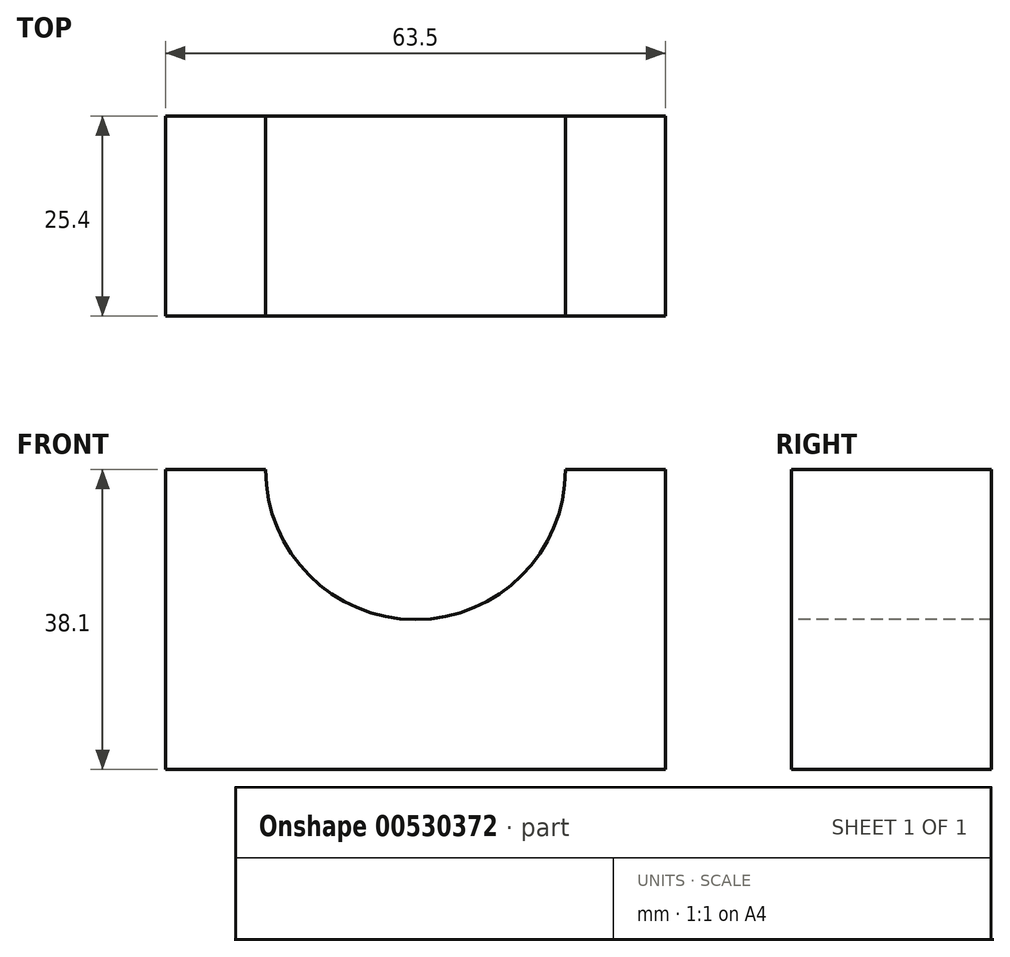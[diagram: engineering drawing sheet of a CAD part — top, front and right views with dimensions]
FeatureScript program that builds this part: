
annotation { "Feature Type Name" : "Feature", "Feature Type Description" : "" }
export const myFeature = defineFeature(function(context is Context, id is Id, definition is map)
    precondition{}
    {
        {
            var Q0;
            Q0=qCreatedBy(makeId("Front.planeOp"),FACE);
            var sketch = newSketch(context, id + "F0", { "sketchPlane" : qUnion([Q0])});
            skLineSegment(sketch, "E0", {"start": v(-63.5, 38.1) * mm, "end": v(-63.5, 0) * mm});
            skLineSegment(sketch, "E1", {"start": v(-63.5, 0) * mm, "end": v(0, 0) * mm});
            skLineSegment(sketch, "E2", {"start": v(0, 0) * mm, "end": v(0, 38.1) * mm});
            skLineSegment(sketch, "E3", {"start": v(0, 38.1) * mm, "end": v(-63.5, 38.1) * mm});
            skSolve(sketch);
        }
        {
            var Q0;
            Q0=makeQuery(id+"F0.imprint","IMPRINT",FACE,{"disambiguationData":[TD([[makeQuery(id+"F0.imprint","IMPRINT",EDGE,{"derivedFrom":sQuery(id+"F0.wireOp",EDGE,"E0")}),1.0]])]});
            extrude(context, id + "F1", {"entities" : qUnion([Q0]), "depth" : 25.4 * mm, "offsetDistance" : 25.4 * mm});
        }
        {
            var Q0;
            Q0=makeQuery(id+"F1.opExtrude","CAP_FACE",FACE,{"disambiguationData":[OSD([sQuery(id+"F0.wireOp",EDGE,"E0"),sQuery(id+"F0.wireOp",EDGE,"E1"),sQuery(id+"F0.wireOp",EDGE,"E2"),sQuery(id+"F0.wireOp",EDGE,"E3")])],"isStart":false});
            var sketch = newSketch(context, id + "F2", { "sketchPlane" : qUnion([Q0])});
            skArc(sketch, "E4", {"start": v(-50.8, 38.1) * mm, "mid": v(-31.75, 19.05) * mm, "end": v(-12.7, 38.1) * mm});
            skSolve(sketch);
        }
        {
            var Q0;
            {var subQ0=sQuery(id+"F2.wireOp",EDGE,"E4");Q0=makeQuery(id+"F2.imprint","IMPRINT",FACE,{"disambiguationData":[TD([[makeQuery(id+"F2.imprint","IMPRINT",EDGE,{"derivedFrom":subQ0}),1.0]])]});}
            extrude(context, id + "F3", {"entities" : qUnion([Q0]), "operationType" : NewBodyOperationType.REMOVE, "endBound" : BoundingType.THROUGH_ALL, "oppositeDirection" : true, "depth" : 25.4 * mm, "offsetDistance" : 25.4 * mm});
        }
    });
